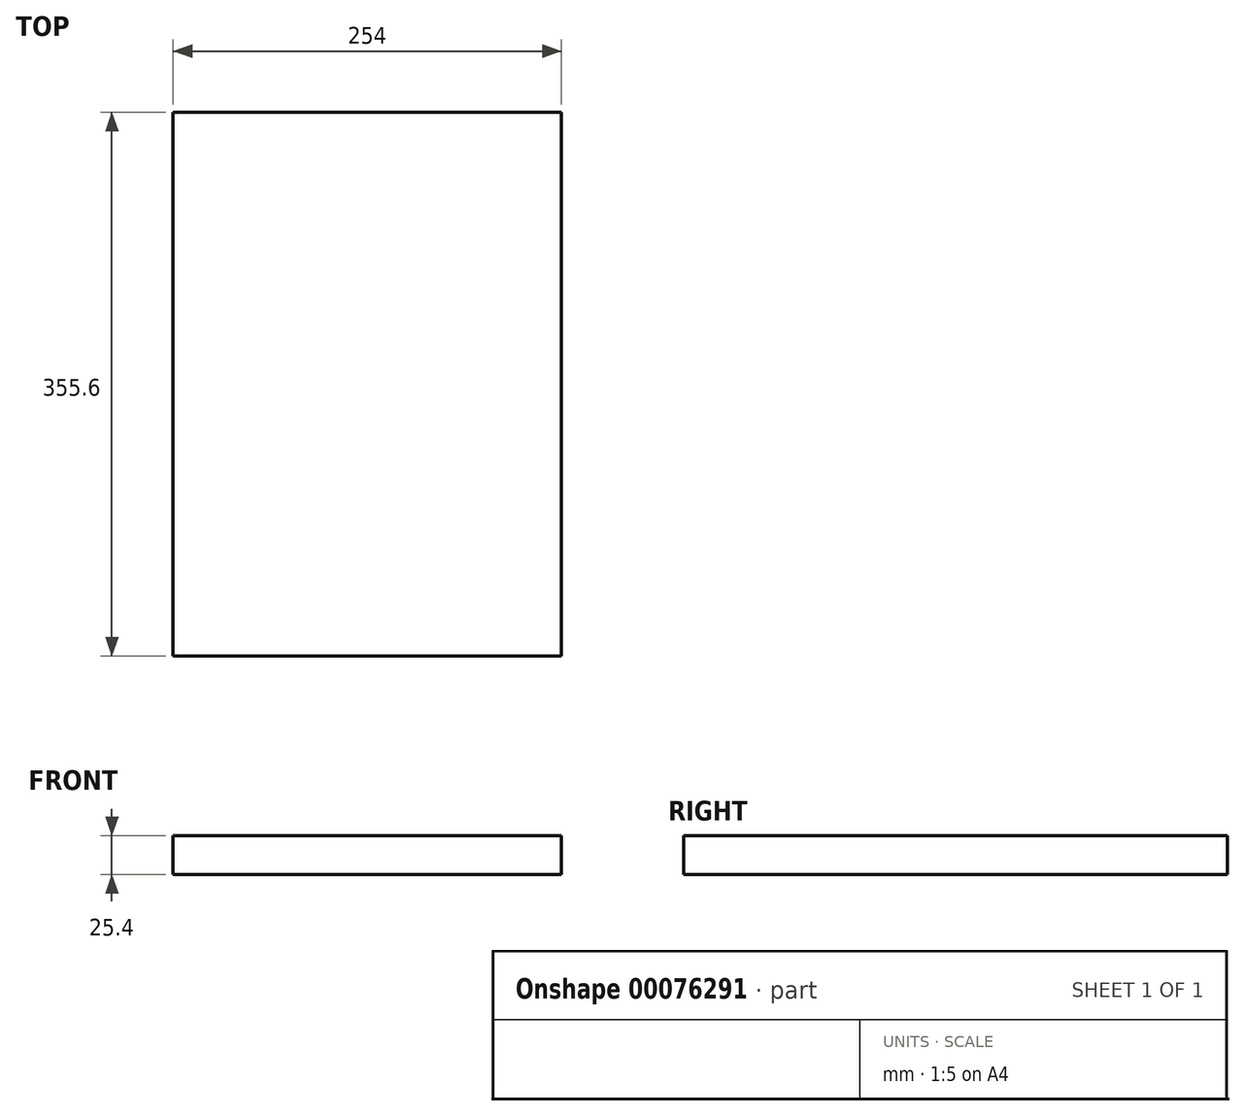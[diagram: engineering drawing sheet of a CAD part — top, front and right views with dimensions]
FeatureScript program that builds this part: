
annotation { "Feature Type Name" : "Feature", "Feature Type Description" : "" }
export const myFeature = defineFeature(function(context is Context, id is Id, definition is map)
    precondition{}
    {
        {
            var Q0;
            Q0=qCreatedBy(makeId("Top.planeOp"),FACE);
            var sketch = newSketch(context, id + "F0", { "sketchPlane" : qUnion([Q0])});
            skLineSegment(sketch, "E0.bottom", {"start": v(-135.86, 256.37) * mm, "end": v(118.14, 256.37) * mm});
            skLineSegment(sketch, "E0.top", {"start": v(-135.86, -99.23) * mm, "end": v(118.14, -99.23) * mm});
            skLineSegment(sketch, "E0.left", {"start": v(-135.86, 256.37) * mm, "end": v(-135.86, -99.23) * mm});
            skLineSegment(sketch, "E0.right", {"start": v(118.14, 256.37) * mm, "end": v(118.14, -99.23) * mm});
            skSolve(sketch);
        }
        {
            var Q0;
            Q0 = qSketchRegion(id + "F0", true);
            extrude(context, id + "F1", {"entities" : qUnion([Q0]), "depth" : 25.4 * mm});
        }
    });
